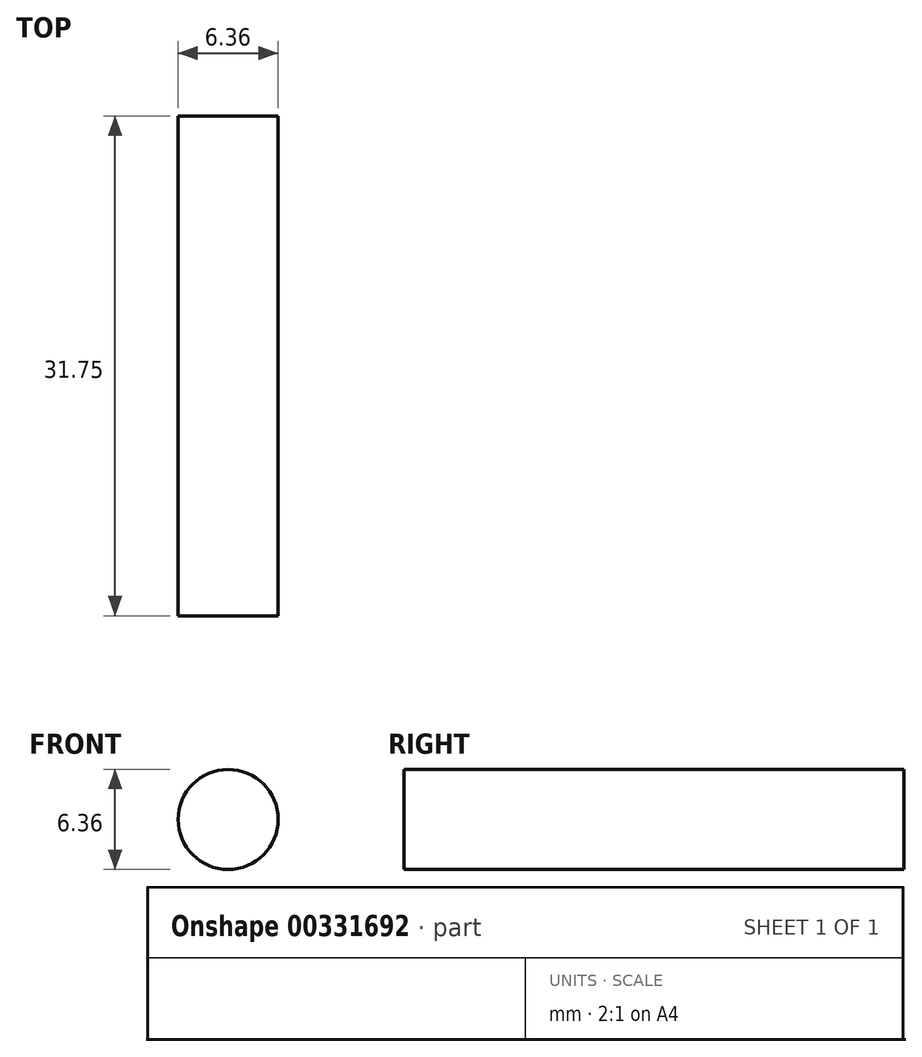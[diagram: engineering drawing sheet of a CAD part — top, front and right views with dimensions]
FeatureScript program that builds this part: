
annotation { "Feature Type Name" : "Feature", "Feature Type Description" : "" }
export const myFeature = defineFeature(function(context is Context, id is Id, definition is map)
    precondition{}
    {
        {
            var Q0;
            Q0=qCreatedBy(makeId("Front.planeOp"),FACE);
            var sketch = newSketch(context, id + "F0", { "sketchPlane" : qUnion([Q0])});
            skCircle(sketch, "E0", {"center": v(0, 0) * mm, "radius": 3.18 * mm});
            skSolve(sketch);
        }
        {
            var Q0;
            Q0 = qSketchRegion(id + "F0", true);
            extrude(context, id + "F1", {"entities" : qUnion([Q0]), "oppositeDirection" : true, "depth" : 31.75 * mm});
        }
    });
